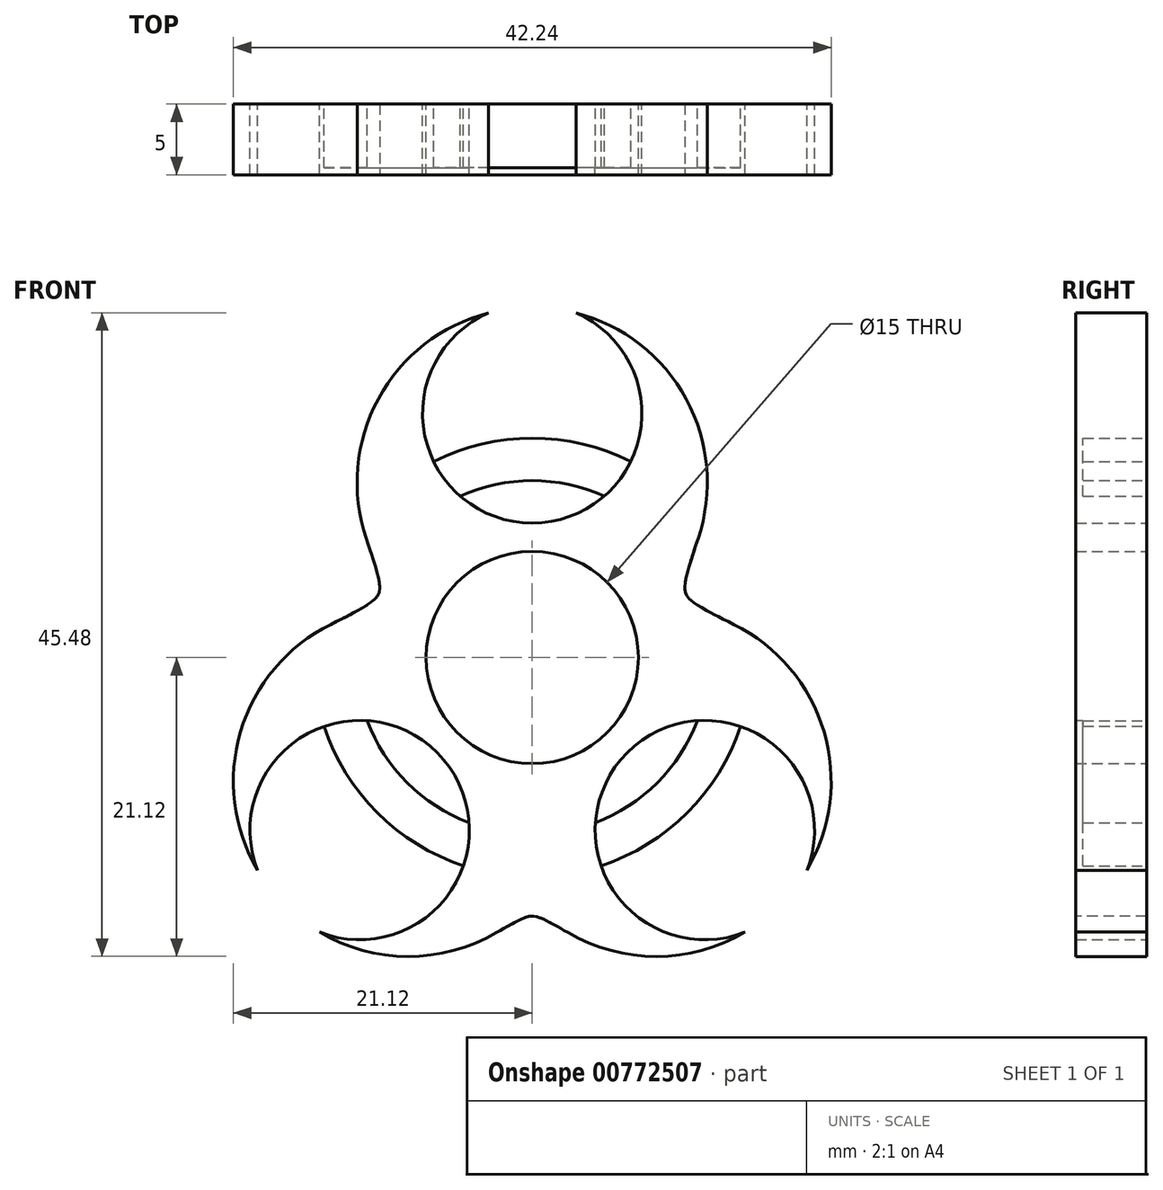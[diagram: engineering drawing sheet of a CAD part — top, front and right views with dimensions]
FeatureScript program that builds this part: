
annotation { "Feature Type Name" : "Feature", "Feature Type Description" : "" }
export const myFeature = defineFeature(function(context is Context, id is Id, definition is map)
    precondition{}
    {
        {
            var Q0;
            Q0=qCreatedBy(makeId("Front.planeOp"),FACE);
            var sketch = newSketch(context, id + "F0", { "sketchPlane" : qUnion([Q0])});
            skLineSegment(sketch, "E0.bottom", {"start": v(25, 25) * mm, "end": v(-25, 25) * mm});
            skLineSegment(sketch, "E0.top", {"start": v(25, -25) * mm, "end": v(-25, -25) * mm});
            skLineSegment(sketch, "E0.left", {"start": v(25, 25) * mm, "end": v(25, -25) * mm});
            skLineSegment(sketch, "E0.right", {"start": v(-25, 25) * mm, "end": v(-25, -25) * mm});
            skPoint(sketch, "E0.middle", {"position": v(0, 0) * mm});
            skPoint(sketch, "E1.second.point", {"position": v(0, 25) * mm});
            skPoint(sketch, "E1.third.point", {"position": v(12.37, 12.37) * mm});
            skArc(sketch, "E2", {"start": v(0, -17.5) * mm, "mid": v(7.2, -21.03) * mm, "end": v(15.04, -19.4) * mm});
            skPoint(sketch, "E2.second.point", {"position": v(17.5, 0) * mm});
            skPoint(sketch, "E2.third.point", {"position": v(0, -17.5) * mm});
            skArc(sketch, "E3", {"start": v(-8.75, 3.62) * mm, "mid": v(-19.5, -2.62) * mm, "end": v(-19.4, -15.04) * mm});
            skPoint(sketch, "E3.third.point", {"position": v(-17.5, 0) * mm});
            skArc(sketch, "E4", {"start": v(8.75, 3.62) * mm, "mid": v(11.94, 15.64) * mm, "end": v(3.09, 24.36) * mm});
            skPoint(sketch, "E4.third.point", {"position": v(-12.37, 12.37) * mm});
            skCircle(sketch, "E5", {"center": v(0, 0) * mm, "radius": 7.5 * mm});
            skArc(sketch, "E6", {"start": v(-3.09, 24.36) * mm, "mid": v(0, 9.5) * mm, "end": v(3.09, 24.36) * mm});
            skArc(sketch, "E7", {"start": v(19.4, -15.04) * mm, "mid": v(6.72, -6.72) * mm, "end": v(15.04, -19.4) * mm});
            skArc(sketch, "E8", {"start": v(-15.04, -19.4) * mm, "mid": v(-6.72, -6.72) * mm, "end": v(-19.4, -15.04) * mm});
            skArc(sketch, "E9.trimOffspring", {"start": v(-15.04, -19.4) * mm, "mid": v(-7.2, -21.03) * mm, "end": v(0, -17.5) * mm});
            skLineSegment(sketch, "E10.trimOffspring", {"start": v(-19.95, -12.2) * mm, "end": v(-20.18, -12.2) * mm});
            skPoint(sketch, "E11.end.orphan", {"position": v(-12, -12) * mm});
            skArc(sketch, "E12.trimOffspring", {"start": v(19.4, -15.04) * mm, "mid": v(19.5, -2.62) * mm, "end": v(8.75, 3.62) * mm});
            skPoint(sketch, "E13.trimOffspring.start.orphan", {"position": v(17.5, -17.5) * mm});
            skPoint(sketch, "E14.start.orphan", {"position": v(0, 24.75) * mm});
            skArc(sketch, "E15.trimOffspring", {"start": v(-3.09, 24.36) * mm, "mid": v(-11.94, 15.64) * mm, "end": v(-8.75, 3.62) * mm});
            skArc(sketch, "E16", {"start": v(-11.68, -4.46) * mm, "mid": v(-8.84, -8.84) * mm, "end": v(-4.46, -11.68) * mm});
            skArc(sketch, "E17", {"start": v(-14.72, -4.87) * mm, "mid": v(-10.96, -10.96) * mm, "end": v(-4.87, -14.72) * mm});
            skArc(sketch, "E18.trimOffspring", {"start": v(4.46, -11.68) * mm, "mid": v(8.84, -8.84) * mm, "end": v(11.68, -4.46) * mm});
            skArc(sketch, "E19.trimOffspring", {"start": v(4.87, -14.72) * mm, "mid": v(10.96, -10.96) * mm, "end": v(14.72, -4.87) * mm});
            skArc(sketch, "E20.trimOffspring", {"start": v(5.1, 11.41) * mm, "mid": v(0, 12.5) * mm, "end": v(-5.1, 11.41) * mm});
            skArc(sketch, "E21.trimOffspring", {"start": v(6.96, 13.85) * mm, "mid": v(0, 15.5) * mm, "end": v(-6.96, 13.85) * mm});
            skSolve(sketch);
        }
        {
            var Q0;
            {var subQ12=sQuery(id+"F0.wireOp",EDGE,"E2");Q0=makeQuery(id+"F0.imprint","IMPRINT",FACE,{"disambiguationData":[TD([[makeQuery(id+"F0.imprint","IMPRINT",EDGE,{"derivedFrom":subQ12}),1.0]])]});}
            extrude(context, id + "F1", {"entities" : qUnion([Q0]), "depth" : 2.5 * mm, "offsetDistance" : 25 * mm, "hasSecondDirection" : true, "secondDirectionOppositeDirection" : true, "secondDirectionDepth" : 2.5 * mm});
        }
        {
            var Q0;
            {var subQ0=sQuery(id+"F0.wireOp",EDGE,"E20.trimOffspring");Q0=makeQuery(id+"F0.imprint","IMPRINT",FACE,{"disambiguationData":[TD([[makeQuery(id+"F0.imprint","IMPRINT",EDGE,{"derivedFrom":subQ0}),-1.0]])]});}
            var Q1;
            {var subQ0=sQuery(id+"F0.wireOp",EDGE,"E18.trimOffspring");Q1=makeQuery(id+"F0.imprint","IMPRINT",FACE,{"disambiguationData":[TD([[makeQuery(id+"F0.imprint","IMPRINT",EDGE,{"derivedFrom":subQ0}),-1.0]])]});}
            var Q2;
            {var subQ0=sQuery(id+"F0.wireOp",EDGE,"E16");Q2=makeQuery(id+"F0.imprint","IMPRINT",FACE,{"disambiguationData":[TD([[makeQuery(id+"F0.imprint","IMPRINT",EDGE,{"derivedFrom":subQ0}),-1.0]])]});}
            extrude(context, id + "F2", {"entities" : qUnion([Q0, Q1, Q2]), "operationType" : NewBodyOperationType.ADD, "depth" : 2 * mm, "offsetDistance" : 25 * mm, "hasSecondDirection" : true, "secondDirectionOppositeDirection" : true, "secondDirectionDepth" : 2.5 * mm});
        }
        {
            var Q0;
            Q0=makeQuery(id+"F1.opExtrude","SWEPT_EDGE",EDGE,{"disambiguationData":[OSD([sQuery(id+"F0.wireOp",EDGE,"E4"),sQuery(id+"F0.wireOp",EDGE,"E12.trimOffspring")])]});
            var Q1;
            Q1=makeQuery(id+"F1.opExtrude","SWEPT_EDGE",EDGE,{"disambiguationData":[OSD([sQuery(id+"F0.wireOp",EDGE,"E3"),sQuery(id+"F0.wireOp",EDGE,"E15.trimOffspring")])]});
            var Q2;
            Q2=makeQuery(id+"F1.opExtrude","SWEPT_EDGE",EDGE,{"disambiguationData":[OSD([sQuery(id+"F0.wireOp",EDGE,"E2"),sQuery(id+"F0.wireOp",EDGE,"E9.trimOffspring")])]});
            fillet(context, id + "F3", {"entities" : qUnion([Q0, Q1, Q2]), "radius" : 5 * mm, "tangentPropagation" : true, "rho" : 0.8, "crossSection" : FilletCrossSection.CONIC, "allowEdgeOverflow" : false});
        }
    });
